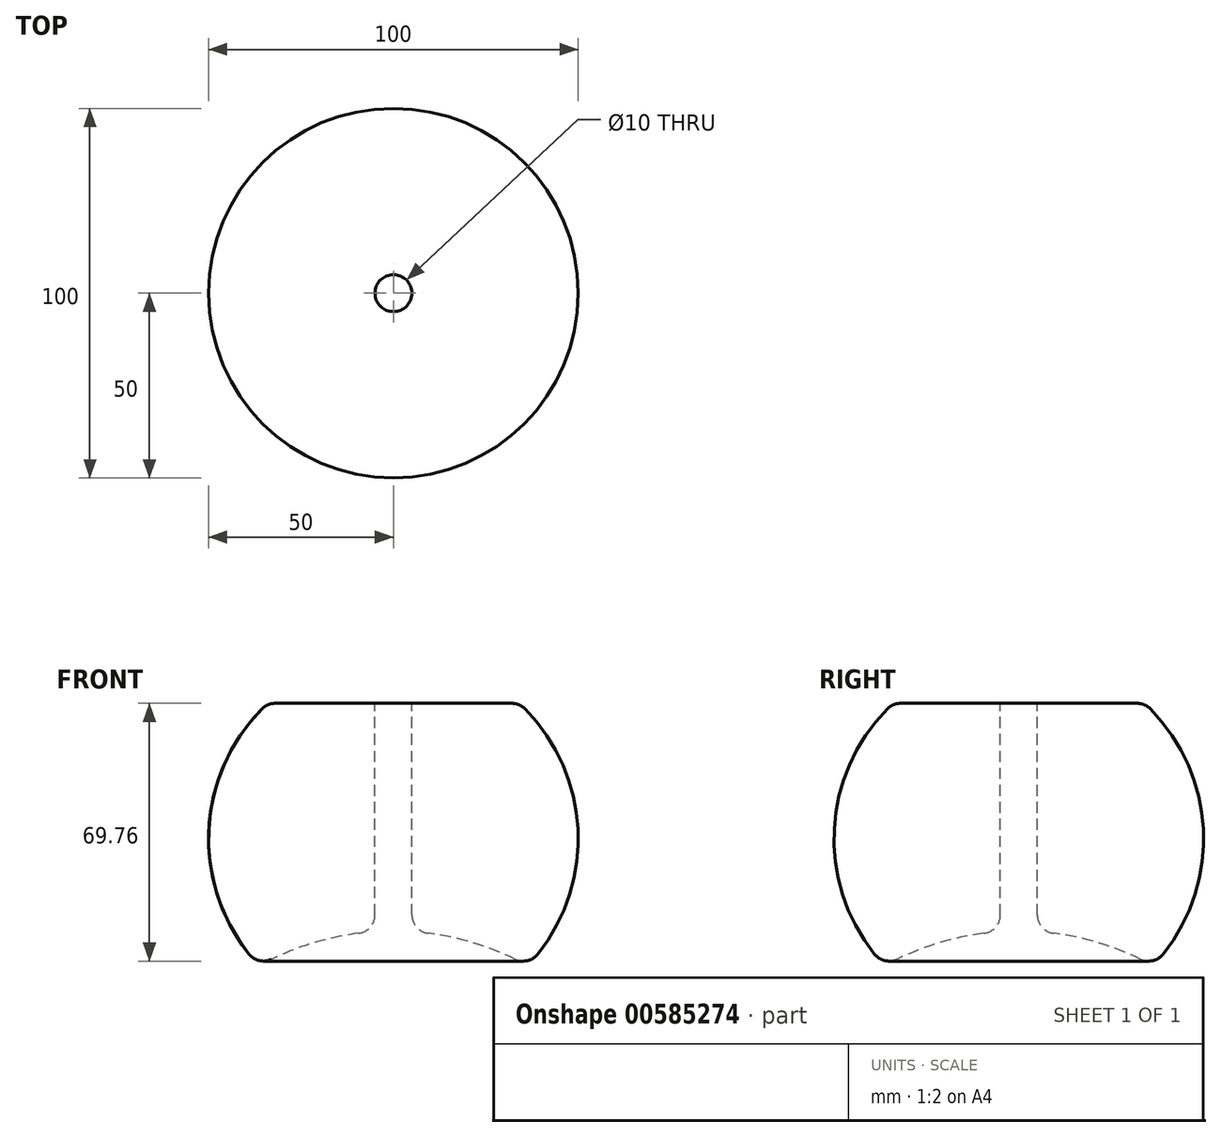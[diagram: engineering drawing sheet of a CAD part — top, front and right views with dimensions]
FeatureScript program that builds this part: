
annotation { "Feature Type Name" : "Feature", "Feature Type Description" : "" }
export const myFeature = defineFeature(function(context is Context, id is Id, definition is map)
    precondition{}
    {
        {
            var Q0;
            Q0=qCreatedBy(makeId("Front.planeOp"),FACE);
            var sketch = newSketch(context, id + "F0", { "sketchPlane" : qUnion([Q0])});
            skArc(sketch, "E0", {"start": v(0, -50) * mm, "mid": v(50, 0) * mm, "end": v(0, 50) * mm});
            skLineSegment(sketch, "E1", {"start": v(0, 50) * mm, "end": v(0, -50) * mm});
            skLineSegment(sketch, "E2", {"start": v(0, 61.5) * mm, "end": v(0, -65.15) * mm, "construction": true});
            skSolve(sketch);
        }
        {
            var Q0;
            Q0 = qSketchRegion(id + "F0", true);
            var Q1;
            Q1=sQuery(id+"F0.wireOp",EDGE,"E2");
            revolve(context, id + "F1", {"entities" : qUnion([Q0]), "axis" : qUnion([Q1]), "revolveType" : RevolveType.FULL});
        }
        {
            var Q0;
            Q0=qCreatedBy(makeId("Front.planeOp"),FACE);
            var sketch = newSketch(context, id + "F2", { "sketchPlane" : qUnion([Q0])});
            skLineSegment(sketch, "E3.bottom", {"start": v(-50, 56.63) * mm, "end": v(50, 56.63) * mm});
            skLineSegment(sketch, "E3.top", {"start": v(-50, 36.63) * mm, "end": v(50, 36.63) * mm});
            skLineSegment(sketch, "E3.left", {"start": v(-50, 56.63) * mm, "end": v(-50, 36.63) * mm});
            skLineSegment(sketch, "E3.right", {"start": v(50, 56.63) * mm, "end": v(50, 36.63) * mm});
            skSolve(sketch);
        }
        {
            var Q0;
            Q0 = qSketchRegion(id + "F2", true);
            extrude(context, id + "F3", {"entities" : qUnion([Q0]), "operationType" : NewBodyOperationType.REMOVE, "endBound" : BoundingType.SYMMETRIC, "depth" : 80 * mm, "offsetDistance" : 25 * mm});
        }
        {
            var Q0;
            Q0=qCreatedBy(makeId("Front.planeOp"),FACE);
            var sketch = newSketch(context, id + "F4", { "sketchPlane" : qUnion([Q0])});
            skArc(sketch, "E4", {"start": v(0, -175) * mm, "mid": v(75, -100) * mm, "end": v(0, -25) * mm});
            skLineSegment(sketch, "E5", {"start": v(0, -25) * mm, "end": v(0, -175) * mm});
            skLineSegment(sketch, "E6", {"start": v(0, -17.78) * mm, "end": v(0, -182.06) * mm, "construction": true});
            skSolve(sketch);
        }
        {
            var Q0;
            Q0=makeQuery(id+"F4.imprint","IMPRINT",FACE,{"disambiguationData":[TD([[makeQuery(id+"F4.imprint","IMPRINT",EDGE,{"derivedFrom":sQuery(id+"F4.wireOp",EDGE,"E4")}),1.0]])]});
            var Q1;
            Q1=sQuery(id+"F4.wireOp",EDGE,"E6");
            revolve(context, id + "F5", {"operationType" : NewBodyOperationType.REMOVE, "entities" : qUnion([Q0]), "axis" : qUnion([Q1]), "revolveType" : RevolveType.FULL, "oppositeDirection" : true});
        }
        {
            var Q0;
            Q0=makeQuery(id+"F3.boolean.opBoolean","COPY",FACE,{"derivedFrom":makeQuery(id+"F3.opExtrude","SWEPT_FACE",FACE,{"disambiguationData":[OSD([sQuery(id+"F2.wireOp",EDGE,"E3.top")])]})});
            var sketch = newSketch(context, id + "F6", { "sketchPlane" : qUnion([Q0])});
            skCircle(sketch, "E7", {"center": v(0, 0) * mm, "radius": 5 * mm});
            skSolve(sketch);
        }
        {
            var Q0;
            Q0 = qSketchRegion(id + "F6", true);
            extrude(context, id + "F7", {"entities" : qUnion([Q0]), "operationType" : NewBodyOperationType.REMOVE, "endBound" : BoundingType.THROUGH_ALL, "oppositeDirection" : true, "depth" : 25 * mm, "offsetDistance" : 25 * mm});
        }
        {
            var Q0;
            Q0=makeQuery(id+"F3.boolean.opBoolean","INTERSECT",EDGE,{"derivedFrom":[makeQuery(id+"F1.opRevolve","SWEPT_FACE",FACE,{"disambiguationData":[OSD([sQuery(id+"F0.wireOp",EDGE,"E0")])]}),makeQuery(id+"F3.opExtrude","SWEPT_FACE",FACE,{"disambiguationData":[OSD([sQuery(id+"F2.wireOp",EDGE,"E3.top")])]})]});
            fillet(context, id + "F8", {"entities" : qUnion([Q0]), "radius" : 5 * mm, "tangentPropagation" : true, "allowEdgeOverflow" : false});
        }
        {
            var Q0;
            Q0=makeQuery(id+"F7.boolean.opBoolean","COPY",EDGE,{"derivedFrom":makeQuery(id+"F7.opExtrude","CAP_EDGE",EDGE,{"disambiguationData":[OSD([sQuery(id+"F6.wireOp",EDGE,"E7")])],"isStart":true})});
            var Q1;
            Q1=makeQuery(id+"F5.boolean.opBoolean","INTERSECT",EDGE,{"derivedFrom":[makeQuery(id+"F1.opRevolve","SWEPT_FACE",FACE,{"disambiguationData":[OSD([sQuery(id+"F0.wireOp",EDGE,"E0")])]}),makeQuery(id+"F5.opRevolve","SWEPT_FACE",FACE,{"disambiguationData":[OSD([sQuery(id+"F4.wireOp",EDGE,"E4")])]})]});
            var Q2;
            Q2=makeQuery(id+"F7.boolean.opBoolean","INTERSECT",EDGE,{"derivedFrom":[makeQuery(id+"F5.boolean.opBoolean","COPY",FACE,{"derivedFrom":makeQuery(id+"F5.opRevolve","SWEPT_FACE",FACE,{"disambiguationData":[OSD([sQuery(id+"F4.wireOp",EDGE,"E4")])]})}),makeQuery(id+"F7.opExtrude","SWEPT_FACE",FACE,{"disambiguationData":[OSD([sQuery(id+"F6.wireOp",EDGE,"E7")])]})]});
            fillet(context, id + "F9", {"entities" : qUnion([Q0, Q1, Q2]), "radius" : 5 * mm, "tangentPropagation" : true, "allowEdgeOverflow" : false});
        }
    });
